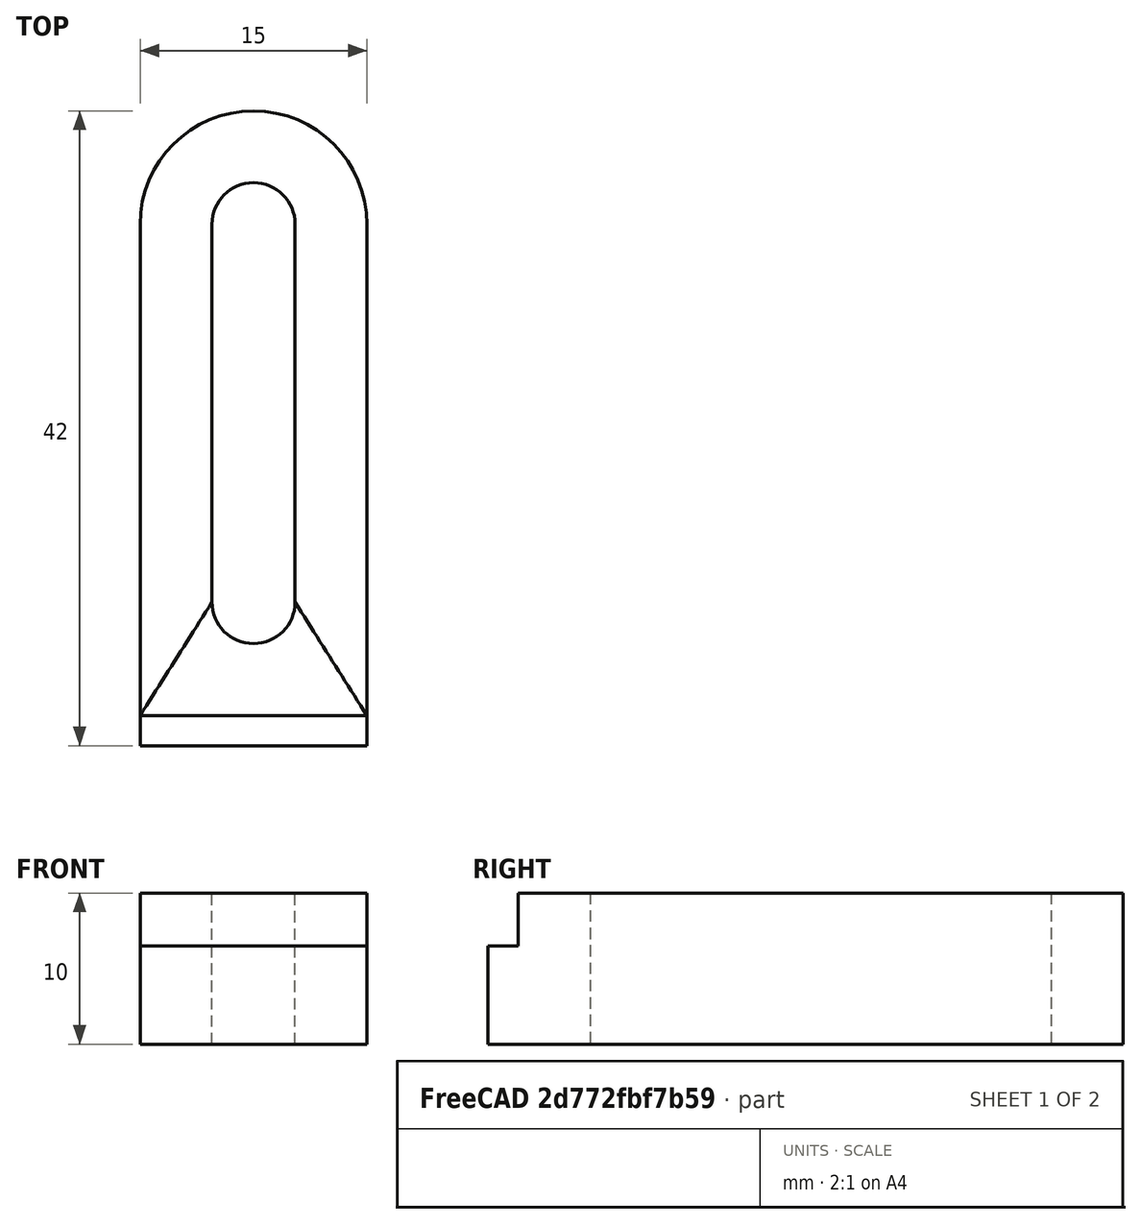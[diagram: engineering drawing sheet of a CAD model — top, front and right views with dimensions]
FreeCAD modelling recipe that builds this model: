
FCSTD DOCUMENT  (FreeCAD 0.14R3702 (Git))
Label: bride_simple
License: CC-BY 3.0
LicenseURL: http://creativecommons.org/licenses/by/3.0/
objects: Part::Feature×12, App::DocumentObjectGroup×4, Part::RuledSurface×4, Part::Extrusion×4, Part::MultiFuse×2, Part::Box×1
note: 23 computed .brp shape members not serialized (recipe doc carries the construction recipe); baked Part::Feature solids carry a one-line shape summary decoded from their .brp

FEATURE [Part::Feature] Line
  shape: bbox 25 x 2e-07 x 2e-07 mm, 0 faces, 0 solids (baked)
FEATURE [Part::Feature] Line001
  shape: bbox 2e-07 x 25 x 2e-07 mm, 0 faces, 0 solids (baked)
FEATURE [Part::Feature] Line002
  shape: bbox 25 x 2e-07 x 2e-07 mm, 0 faces, 0 solids (baked)
FEATURE [Part::Feature] Line003
  shape: bbox 2e-07 x 25 x 2e-07 mm, 0 faces, 0 solids (baked)
FEATURE [App::DocumentObjectGroup] _  label="0"
  Group = -> [Line,Line001,Line002,Line003]
FEATURE [Part::Feature] Line004
  shape: bbox 15 x 2e-07 x 2e-07 mm, 0 faces, 0 solids (baked)
FEATURE [Part::Feature] Line005
  shape: bbox 2e-07 x 32.5 x 2e-07 mm, 0 faces, 0 solids (baked)
FEATURE [Part::Feature] Line006
  shape: bbox 2e-07 x 32.5 x 2e-07 mm, 0 faces, 0 solids (baked)
FEATURE [Part::Feature] Line007
  shape: bbox 2e-07 x 25 x 2e-07 mm, 0 faces, 0 solids (baked)
FEATURE [Part::Feature] Line008
  shape: bbox 2e-07 x 25 x 2e-07 mm, 0 faces, 0 solids (baked)
FEATURE [Part::Feature] Arc
  shape: bbox 15 x 7.5 x 2e-07 mm, 0 faces, 0 solids (baked)
FEATURE [App::DocumentObjectGroup] exterieur
  Group = -> [Line004,Line005,Line006,Arc]
FEATURE [Part::Feature] Arc001
  shape: bbox 5.5 x 2.75 x 2e-07 mm, 0 faces, 0 solids (baked)
FEATURE [Part::Feature] Arc002
  shape: bbox 5.5 x 2.75 x 2e-07 mm, 0 faces, 0 solids (baked)
FEATURE [App::DocumentObjectGroup] interieur
  Group = -> [Line007,Line008,Arc001,Arc002]
FEATURE [App::DocumentObjectGroup] pince_fr
  Group = -> [_,exterieur,interieur]
FEATURE [Part::RuledSurface] Ruled_Surface
  Curve1 = -> Arc001 [Edge1]
  Curve2 = -> Arc [Edge1]
  Orientation = 0
FEATURE [Part::RuledSurface] Ruled_Surface001
  Curve1 = -> Line008 [Edge1]
  Curve2 = -> Line006 [Edge1]
  Orientation = 0
FEATURE [Part::RuledSurface] Ruled_Surface002
  Curve1 = -> Arc002 [Edge1]
  Curve2 = -> Line004 [Edge1]
  Orientation = 0
FEATURE [Part::RuledSurface] Ruled_Surface003
  Curve1 = -> Line007 [Edge1]
  Curve2 = -> Line005 [Edge1]
  Orientation = 0
FEATURE [Part::Extrusion] Extrude
  Base = -> Ruled_Surface
  Dir = (0,0,10)
  Solid = false
FEATURE [Part::Extrusion] Extrude001
  Base = -> Ruled_Surface001
  Dir = (0,0,10)
  Solid = false
FEATURE [Part::Extrusion] Extrude002
  Base = -> Ruled_Surface002
  Dir = (0,0,10)
  Solid = false
FEATURE [Part::Extrusion] Extrude003
  Base = -> Ruled_Surface003
  Dir = (0,0,10)
  Solid = false
FEATURE [Part::Box] Box  label="fente"
  Height = 6.5
  Length = 15
  Placement = pos=(17.5,15.5,0) rot=(0,0,1;0rad)
  Width = 2
FEATURE [Part::MultiFuse] Fusion001
  Shapes = -> [Extrude,Extrude001,Extrude002,Extrude003]
FEATURE [Part::MultiFuse] Fusion002  label="Bride"
  Shapes = -> [Box,Fusion001]
